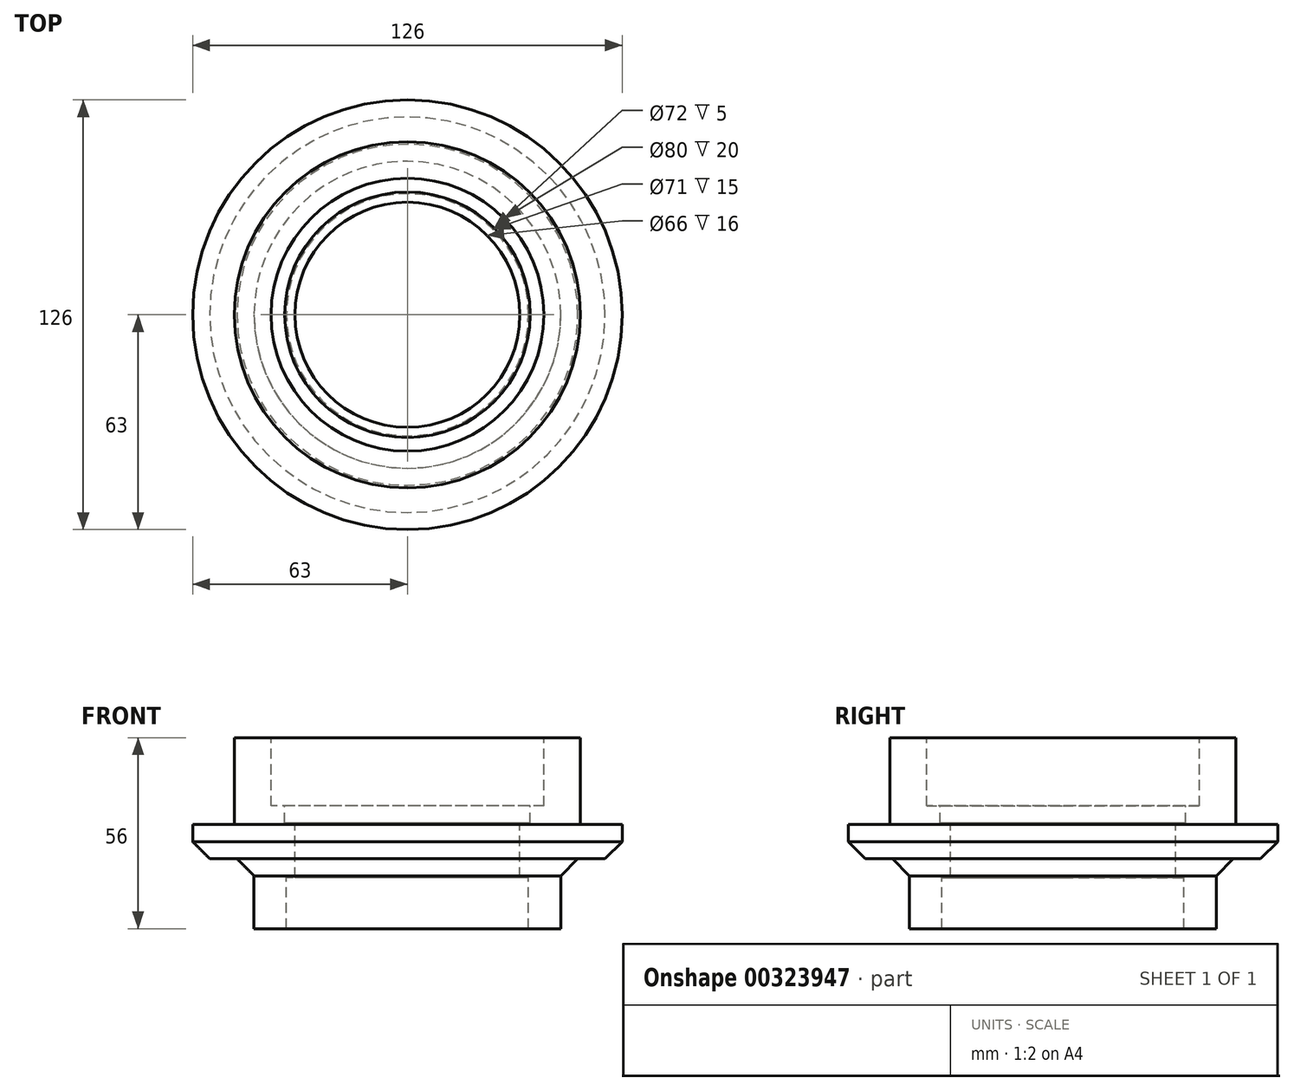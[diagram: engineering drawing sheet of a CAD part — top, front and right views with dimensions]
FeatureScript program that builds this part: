
annotation { "Feature Type Name" : "Feature", "Feature Type Description" : "" }
export const myFeature = defineFeature(function(context is Context, id is Id, definition is map)
    precondition{}
    {
        {
            var Q0;
            Q0=qCreatedBy(makeId("Front.planeOp"),FACE);
            var sketch = newSketch(context, id + "F0", { "sketchPlane" : qUnion([Q0])});
            skLineSegment(sketch, "E0", {"start": v(0, 0) * mm, "end": v(40, 0) * mm});
            skLineSegment(sketch, "E1", {"start": v(40, 0) * mm, "end": v(40, -20) * mm});
            skLineSegment(sketch, "E2", {"start": v(40, -20) * mm, "end": v(0, -20) * mm});
            skLineSegment(sketch, "E3", {"start": v(0, -20) * mm, "end": v(0, -25) * mm});
            skLineSegment(sketch, "E4", {"start": v(0, -25) * mm, "end": v(36, -25) * mm});
            skLineSegment(sketch, "E5", {"start": v(36, -25) * mm, "end": v(36, -20) * mm});
            skLineSegment(sketch, "E6", {"start": v(0, -25) * mm, "end": v(33, -25) * mm});
            skLineSegment(sketch, "E7", {"start": v(33, -25) * mm, "end": v(33, -41) * mm});
            skLineSegment(sketch, "E8", {"start": v(33, -41) * mm, "end": v(0, -41) * mm});
            skLineSegment(sketch, "E9", {"start": v(0, -41) * mm, "end": v(0, -56) * mm});
            skLineSegment(sketch, "E10", {"start": v(0, -56) * mm, "end": v(35.5, -56) * mm});
            skLineSegment(sketch, "E11", {"start": v(35.5, -56) * mm, "end": v(35.5, -41) * mm});
            skLineSegment(sketch, "E12", {"start": v(35.5, -41) * mm, "end": v(33, -41) * mm});
            skLineSegment(sketch, "E13", {"start": v(40, 0) * mm, "end": v(50.75, 0) * mm});
            skLineSegment(sketch, "E14", {"start": v(50.75, 0) * mm, "end": v(50.75, -25.5) * mm});
            skLineSegment(sketch, "E15", {"start": v(50.75, -25.5) * mm, "end": v(63, -25.5) * mm});
            skLineSegment(sketch, "E16", {"start": v(63, -25.5) * mm, "end": v(63, -35.5) * mm});
            skLineSegment(sketch, "E17", {"start": v(63, -35.5) * mm, "end": v(45, -35.5) * mm});
            skLineSegment(sketch, "E18", {"start": v(45, -35.5) * mm, "end": v(45, -56) * mm});
            skLineSegment(sketch, "E19", {"start": v(45, -56) * mm, "end": v(35.5, -56) * mm});
            skLineSegment(sketch, "E20", {"start": v(0, 0) * mm, "end": v(0, -56) * mm});
            skLineSegment(sketch, "E21.MirrorCS", {"start": v(-35.5, -41) * mm, "end": v(-33, -41) * mm});
            skLineSegment(sketch, "E22.MirrorCS", {"start": v(-36, -25) * mm, "end": v(-36, -20) * mm});
            skLineSegment(sketch, "E23.MirrorCS", {"start": v(0, -25) * mm, "end": v(-36, -25) * mm});
            skLineSegment(sketch, "E24.MirrorCS", {"start": v(-63, -35.5) * mm, "end": v(-45, -35.5) * mm});
            skLineSegment(sketch, "E25.MirrorCS", {"start": v(-50.75, 0) * mm, "end": v(-50.75, -25.5) * mm});
            skLineSegment(sketch, "E26.MirrorCS", {"start": v(-50.75, -25.5) * mm, "end": v(-63, -25.5) * mm});
            skLineSegment(sketch, "E27.MirrorCS", {"start": v(0, 0) * mm, "end": v(-40, 0) * mm});
            skLineSegment(sketch, "E28.MirrorCS", {"start": v(-40, 0) * mm, "end": v(-40, -20) * mm});
            skLineSegment(sketch, "E29.MirrorCS", {"start": v(-40, 0) * mm, "end": v(-50.75, 0) * mm});
            skLineSegment(sketch, "E30.MirrorCS", {"start": v(-33, -41) * mm, "end": v(0, -41) * mm});
            skLineSegment(sketch, "E31.MirrorCS", {"start": v(-40, -20) * mm, "end": v(0, -20) * mm});
            skLineSegment(sketch, "E32.MirrorCS", {"start": v(0, -56) * mm, "end": v(-35.5, -56) * mm});
            skLineSegment(sketch, "E33.MirrorCS", {"start": v(-35.5, -56) * mm, "end": v(-35.5, -41) * mm});
            skLineSegment(sketch, "E34.MirrorCS", {"start": v(-33, -25) * mm, "end": v(-33, -41) * mm});
            skLineSegment(sketch, "E35.MirrorCS", {"start": v(0, -25) * mm, "end": v(-33, -25) * mm});
            skLineSegment(sketch, "E36.MirrorCS", {"start": v(-45, -56) * mm, "end": v(-35.5, -56) * mm});
            skLineSegment(sketch, "E37.MirrorCS", {"start": v(-45, -35.5) * mm, "end": v(-45, -56) * mm});
            skLineSegment(sketch, "E38.MirrorCS", {"start": v(-63, -25.5) * mm, "end": v(-63, -35.5) * mm});
            skSolve(sketch);
        }
        {
            var Q0;
            Q0=makeQuery(id+"F0.imprint","IMPRINT",FACE,{"disambiguationData":[TD([[makeQuery(id+"F0.imprint","IMPRINT",EDGE,{"derivedFrom":sQuery(id+"F0.wireOp",EDGE,"E21.MirrorCS")}),1.0]])]});
            var Q1;
            Q1=sQuery(id+"F0.wireOp",EDGE,"E20");
            revolve(context, id + "F1", {"entities" : qUnion([Q0]), "axis" : qUnion([Q1]), "revolveType" : RevolveType.FULL});
        }
        {
            var Q0;
            Q0=makeQuery(id+"F1.opRevolve","SWEPT_FACE",FACE,{"disambiguationData":[OSD([sQuery(id+"F0.wireOp",EDGE,"E24.MirrorCS")])]});
            chamfer(context, id + "F2", {"entities" : qUnion([Q0]), "width" : 5 * mm, "tangentPropagation" : true});
        }
    });
